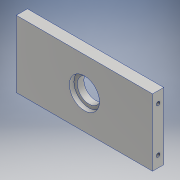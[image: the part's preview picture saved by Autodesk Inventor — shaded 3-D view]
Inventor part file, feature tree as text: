
AUTODESK INVENTOR PART (.ipt)
format: ipt  version: 2018 (Build 220112000, 112)  size: 131,072 bytes
history: native  units: mm
features: sketch x5, extrude x3, hole x2, other x1
ambient origin geometry x8: Origin, YZ Plane, XZ Plane, XY Plane, X Axis, Y Axis, Z Axis, Center Point
bodies: Body1 (feature_tree)
feature tree (11):
  other  "ソリッド1"
  extrude  "押し出し1"  Depth=60.0mm
  extrude  "押し出し2"  Depth=122.057mm
  extrude  "押し出し4"  Depth=10.0mm TaperAngle=0.0deg
  hole  "穴1"  [1 undecoded]
  hole  "穴2"  [1 undecoded]
  sketch  "スケッチ1"
  sketch  "スケッチ2"
  sketch  "スケッチ3"
  sketch  "スケッチ4"
  sketch  "スケッチ5"
note: 2 required parameter values undecoded (feature->parameter linkage not recoverable at this tier; creation-order binding heuristic only, values carry confidence <= 0.55)
